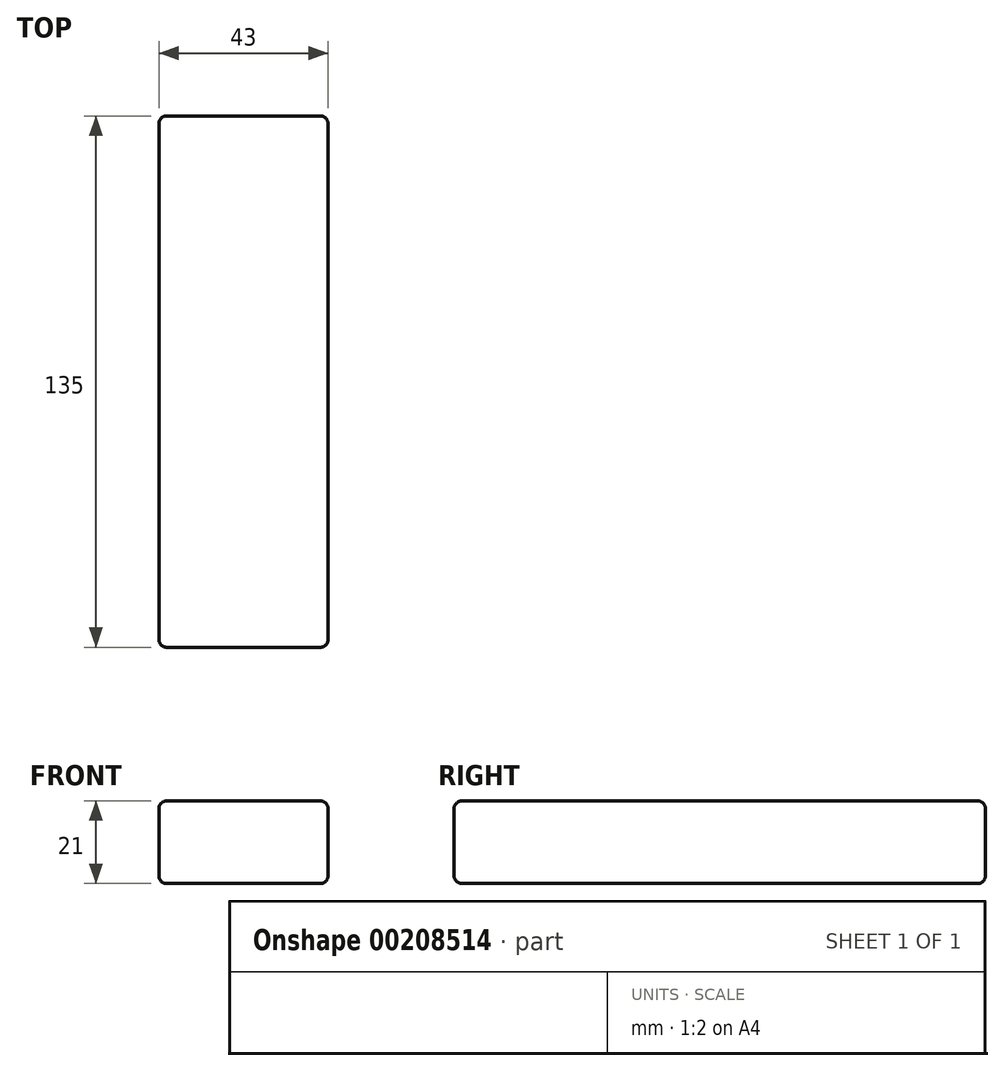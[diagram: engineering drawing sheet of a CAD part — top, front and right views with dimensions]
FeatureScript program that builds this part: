
annotation { "Feature Type Name" : "Feature", "Feature Type Description" : "" }
export const myFeature = defineFeature(function(context is Context, id is Id, definition is map)
    precondition{}
    {
        {
            var Q0;
            Q0=qCreatedBy(makeId("Top.planeOp"),FACE);
            var sketch = newSketch(context, id + "F0", { "sketchPlane" : qUnion([Q0])});
            skLineSegment(sketch, "E0.bottom", {"start": v(21.5, 67.5) * mm, "end": v(-21.5, 67.5) * mm});
            skLineSegment(sketch, "E0.top", {"start": v(21.5, -67.5) * mm, "end": v(-21.5, -67.5) * mm});
            skLineSegment(sketch, "E0.left", {"start": v(21.5, 67.5) * mm, "end": v(21.5, -67.5) * mm});
            skLineSegment(sketch, "E0.right", {"start": v(-21.5, 67.5) * mm, "end": v(-21.5, -67.5) * mm});
            skPoint(sketch, "E0.middle", {"position": v(0, 0) * mm});
            skSolve(sketch);
        }
        {
            var Q0;
            Q0 = qSketchRegion(id + "F0", true);
            extrude(context, id + "F1", {"entities" : qUnion([Q0]), "endBound" : BoundingType.SYMMETRIC, "depth" : 21 * mm});
        }
        {
            var Q0;
            Q0=makeQuery(id+"F1.opExtrude","CAP_FACE",FACE,{"disambiguationData":[OSD([sQuery(id+"F0.wireOp",EDGE,"E0.bottom"),sQuery(id+"F0.wireOp",EDGE,"E0.top"),sQuery(id+"F0.wireOp",EDGE,"E0.left"),sQuery(id+"F0.wireOp",EDGE,"E0.right")])],"isStart":false});
            var Q1;
            Q1=makeQuery(id+"F1.opExtrude","CAP_FACE",FACE,{"disambiguationData":[OSD([sQuery(id+"F0.wireOp",EDGE,"E0.bottom"),sQuery(id+"F0.wireOp",EDGE,"E0.top"),sQuery(id+"F0.wireOp",EDGE,"E0.left"),sQuery(id+"F0.wireOp",EDGE,"E0.right")])],"isStart":true});
            var Q2;
            Q2=makeQuery(id+"F1.opExtrude","SWEPT_FACE",FACE,{"disambiguationData":[OSD([sQuery(id+"F0.wireOp",EDGE,"E0.left")])]});
            var Q3;
            Q3=makeQuery(id+"F1.opExtrude","SWEPT_FACE",FACE,{"disambiguationData":[OSD([sQuery(id+"F0.wireOp",EDGE,"E0.top")])]});
            var Q4;
            Q4=makeQuery(id+"F1.opExtrude","SWEPT_FACE",FACE,{"disambiguationData":[OSD([sQuery(id+"F0.wireOp",EDGE,"E0.bottom")])]});
            var Q5;
            Q5=makeQuery(id+"F1.opExtrude","SWEPT_FACE",FACE,{"disambiguationData":[OSD([sQuery(id+"F0.wireOp",EDGE,"E0.right")])]});
            fillet(context, id + "F2", {"entities" : qUnion([Q0, Q1, Q2, Q3, Q4, Q5]), "radius" : 2 * mm, "tangentPropagation" : true, "allowEdgeOverflow" : false});
        }
    });
